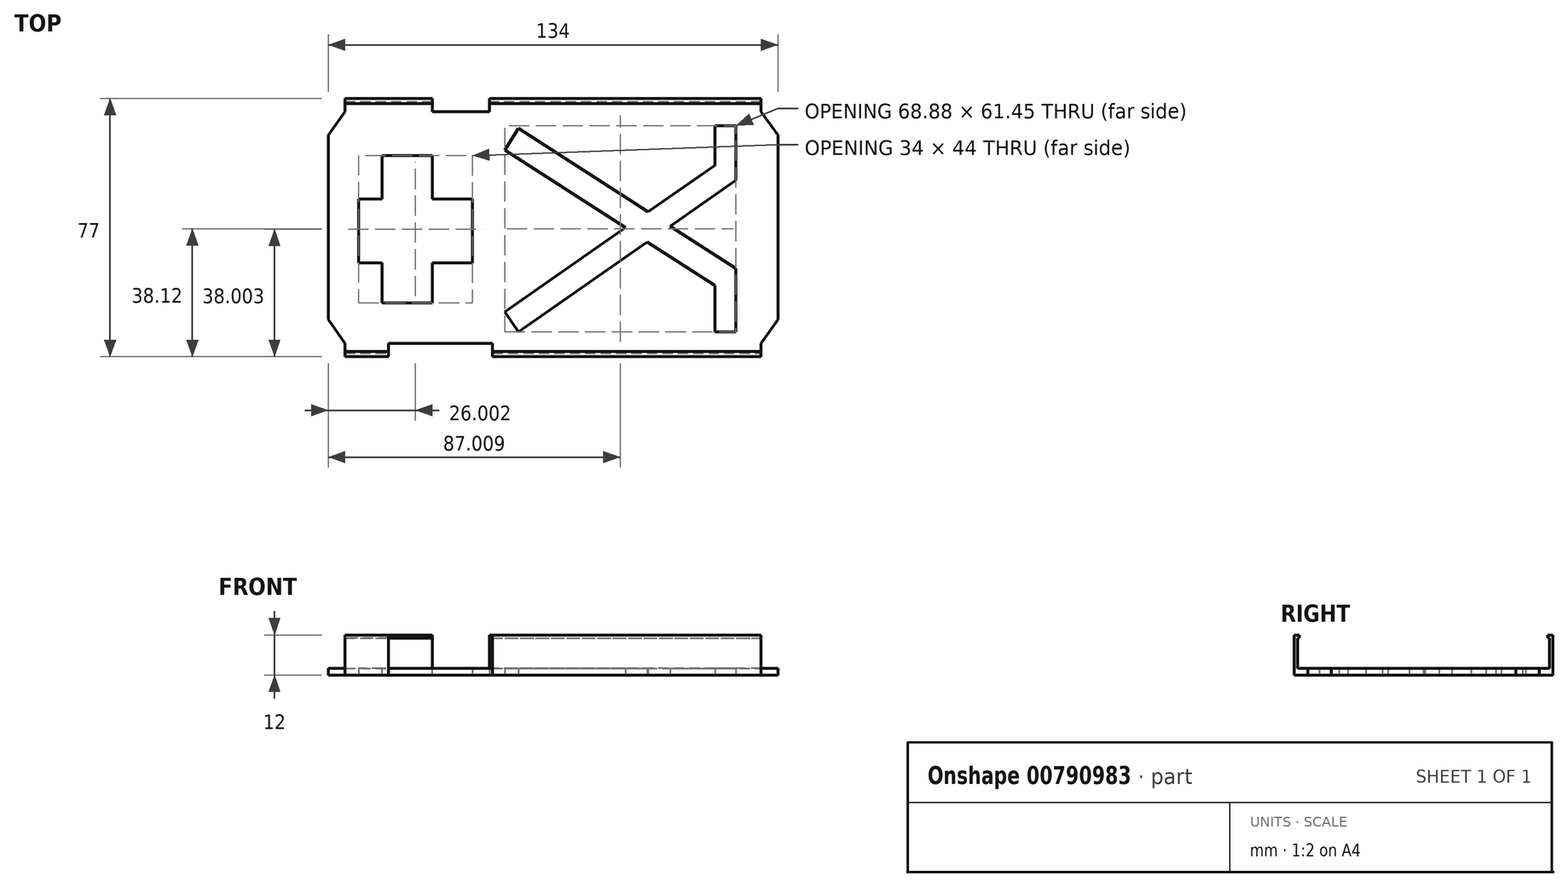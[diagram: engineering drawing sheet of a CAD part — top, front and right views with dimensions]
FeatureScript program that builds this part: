
annotation { "Feature Type Name" : "Feature", "Feature Type Description" : "" }
export const myFeature = defineFeature(function(context is Context, id is Id, definition is map)
    precondition{}
    {
        {
            var Q0;
            Q0=qCreatedBy(makeId("Top.planeOp"),FACE);
            var sketch = newSketch(context, id + "F0", { "sketchPlane" : qUnion([Q0])});
            skLineSegment(sketch, "E0.bottom", {"start": v(-71.89, 59.7) * mm, "end": v(62.11, 59.7) * mm});
            skLineSegment(sketch, "E0.top", {"start": v(-71.89, -9.3) * mm, "end": v(62.11, -9.3) * mm});
            skLineSegment(sketch, "E0.left", {"start": v(-71.89, 59.7) * mm, "end": v(-71.89, -9.3) * mm});
            skLineSegment(sketch, "E0.right", {"start": v(62.11, 59.7) * mm, "end": v(62.11, -9.3) * mm});
            skPoint(sketch, "E1", {"position": v(-71.89, 25.2) * mm});
            skSolve(sketch);
        }
        {
            var Q0;
            Q0=makeQuery(id+"F0.imprint","IMPRINT",FACE,{"disambiguationData":[TD([[makeQuery(id+"F0.imprint","IMPRINT",EDGE,{"derivedFrom":sQuery(id+"F0.wireOp",EDGE,"E0.bottom")}),-1.0]])]});
            extrude(context, id + "F1", {"entities" : qUnion([Q0]), "depth" : 2 * mm, "offsetDistance" : 25 * mm});
        }
        {
            var Q0;
            Q0=makeQuery(id+"F1.opExtrude","SWEPT_FACE",FACE,{"disambiguationData":[OSD([sQuery(id+"F0.wireOp",EDGE,"E0.top")])]});
            var sketch = newSketch(context, id + "F2", { "sketchPlane" : qUnion([Q0])});
            skLineSegment(sketch, "E2.bottom", {"start": v(57.11, 2) * mm, "end": v(-23.89, 2) * mm});
            skLineSegment(sketch, "E2.top", {"start": v(57.11, 0) * mm, "end": v(-23.89, 0) * mm});
            skLineSegment(sketch, "E2.left", {"start": v(57.11, 2) * mm, "end": v(57.11, 0) * mm});
            skLineSegment(sketch, "E2.right", {"start": v(-23.89, 2) * mm, "end": v(-23.89, 0) * mm});
            skSolve(sketch);
        }
        {
            var Q0;
            Q0=makeQuery(id+"F2.imprint","IMPRINT",FACE,{"disambiguationData":[TD([[makeQuery(id+"F2.imprint","IMPRINT",EDGE,{"derivedFrom":sQuery(id+"F2.wireOp",EDGE,"E2.bottom")}),-1.0]])]});
            extrude(context, id + "F3", {"entities" : qUnion([Q0]), "operationType" : NewBodyOperationType.ADD, "depth" : 4 * mm, "offsetDistance" : 25 * mm});
        }
        {
            var Q0;
            Q0=makeQuery(id+"F3.boolean.opBoolean","MERGE",FACE,{"derivedFrom":[makeQuery(id+"F1.opExtrude","CAP_FACE",FACE,{"disambiguationData":[OSD([sQuery(id+"F0.wireOp",EDGE,"E0.bottom"),sQuery(id+"F0.wireOp",EDGE,"E0.top"),sQuery(id+"F0.wireOp",EDGE,"E0.left"),sQuery(id+"F0.wireOp",EDGE,"E0.right")])],"isStart":false}),makeQuery(id+"F3.opExtrude","SWEPT_FACE",FACE,{"disambiguationData":[OSD([sQuery(id+"F2.wireOp",EDGE,"E2.bottom")])]})]});
            var sketch = newSketch(context, id + "F4", { "sketchPlane" : qUnion([Q0])});
            skLineSegment(sketch, "E3", {"start": v(-23.89, -9.3) * mm, "end": v(57.11, -9.3) * mm});
            skSolve(sketch);
        }
        {
            var Q0;
            Q0=makeQuery(id+"F4.imprint","IMPRINT",FACE,{"disambiguationData":[TD([[makeQuery(id+"F4.imprint","IMPRINT",EDGE,{"derivedFrom":sQuery(id+"F4.wireOp",EDGE,"E3")}),-1.0]])]});
            extrude(context, id + "F5", {"entities" : qUnion([Q0]), "operationType" : NewBodyOperationType.ADD, "depth" : 3 * mm, "offsetDistance" : 25 * mm});
        }
        {
            var Q0;
            Q0=makeQuery(id+"F5.opExtrude","CAP_FACE",FACE,{"disambiguationData":[OSD([sQuery(id+"F0.wireOp",EDGE,"E0.top"),sQuery(id+"F2.wireOp",EDGE,"E2.bottom"),sQuery(id+"F2.wireOp",EDGE,"E2.left"),sQuery(id+"F2.wireOp",EDGE,"E2.right"),sQuery(id+"F4.wireOp",EDGE,"E3")])],"isStart":false});
            extrude(context, id + "F6", {"entities" : qUnion([Q0]), "operationType" : NewBodyOperationType.ADD, "depth" : 7 * mm, "offsetDistance" : 25 * mm});
        }
        {
            var Q0;
            {var subQ0=sQuery(id+"F4.wireOp",EDGE,"E3");Q0=makeQuery(id+"F6.boolean.opBoolean","MERGE",FACE,{"derivedFrom":[makeQuery(id+"F5.opExtrude","SWEPT_FACE",FACE,{"disambiguationData":[OSD([subQ0])]}),makeQuery(id+"F6.opExtrude","SWEPT_FACE",FACE,{"disambiguationData":[OSD([subQ0])]})]});}
            extrude(context, id + "F7", {"entities" : qUnion([Q0]), "operationType" : NewBodyOperationType.REMOVE, "oppositeDirection" : true, "depth" : 3 * mm, "offsetDistance" : 25 * mm});
        }
        {
            var Q0;
            Q0=makeQuery(id+"F7.boolean.opBoolean","COPY",FACE,{"derivedFrom":makeQuery(id+"F7.opExtrude","CAP_FACE",FACE,{"disambiguationData":[OSD([sQuery(id+"F4.wireOp",EDGE,"E3")])],"isStart":false})});
            var sketch = newSketch(context, id + "F8", { "sketchPlane" : qUnion([Q0])});
            skLineSegment(sketch, "E4", {"start": v(-57.11, 12) * mm, "end": v(23.89, 12) * mm});
            skLineSegment(sketch, "E5", {"start": v(23.89, 12) * mm, "end": v(23.89, 11) * mm});
            skLineSegment(sketch, "E6", {"start": v(23.89, 11) * mm, "end": v(-57.11, 11) * mm});
            skLineSegment(sketch, "E7", {"start": v(-57.11, 11) * mm, "end": v(-57.11, 12) * mm});
            skSolve(sketch);
        }
        {
            var Q0;
            Q0=makeQuery(id+"F8.imprint","IMPRINT",FACE,{"disambiguationData":[TD([[makeQuery(id+"F8.imprint","IMPRINT",EDGE,{"derivedFrom":sQuery(id+"F8.wireOp",EDGE,"E4")}),1.0]])]});
            extrude(context, id + "F9", {"entities" : qUnion([Q0]), "operationType" : NewBodyOperationType.ADD, "depth" : 0.5 * mm, "offsetDistance" : 25 * mm});
        }
        {
            var Q0;
            {var subQ0=sQuery(id+"F2.wireOp",EDGE,"E2.right");var subQ1=sQuery(id+"F2.wireOp",EDGE,"E2.bottom");var subQ2=sQuery(id+"F0.wireOp",EDGE,"E0.top");Q0=makeQuery(id+"F9.boolean.opBoolean","MERGE",FACE,{"derivedFrom":[makeQuery(id+"F6.boolean.opBoolean","MERGE",FACE,{"derivedFrom":[makeQuery(id+"F5.boolean.opBoolean","MERGE",FACE,{"derivedFrom":[makeQuery(id+"F3.opExtrude","SWEPT_FACE",FACE,{"disambiguationData":[OSD([subQ0])]}),makeQuery(id+"F5.opExtrude","SWEPT_FACE",FACE,{"disambiguationData":[OSD([subQ2,subQ1,subQ0])]})]}),makeQuery(id+"F6.opExtrude","SWEPT_FACE",FACE,{"disambiguationData":[OSD([subQ2,subQ1,subQ0])]})]}),makeQuery(id+"F9.opExtrude","SWEPT_FACE",FACE,{"disambiguationData":[OSD([sQuery(id+"F8.wireOp",EDGE,"zQEFb7VZ-tBJw-V2n3-Wt8e-xeAuR17gCr9D.right")])]})]});}
            extrude(context, id + "F10", {"entities" : qUnion([Q0]), "operationType" : NewBodyOperationType.REMOVE, "oppositeDirection" : true, "depth" : 1 * mm, "offsetDistance" : 25 * mm});
        }
        {
            var Q0;
            {var subQ0=sQuery(id+"F2.wireOp",EDGE,"E2.right");var subQ2=sQuery(id+"F0.wireOp",EDGE,"E0.left");var subQ3=sQuery(id+"F0.wireOp",EDGE,"E0.top");Q0=makeQuery(id+"F10.boolean.opBoolean","MERGE",FACE,{"derivedFrom":[makeQuery(id+"F3.boolean.opBoolean","SPLIT",FACE,{"disambiguationData":[TD([makeQuery(id+"F1.opExtrude","SWEPT_FACE",FACE,{"disambiguationData":[OSD([subQ2])]})])],"derivedFrom":makeQuery(id+"F1.opExtrude","SWEPT_FACE",FACE,{"disambiguationData":[OSD([subQ3])]})}),makeQuery(id+"F10.opExtrude","SWEPT_FACE",FACE,{"disambiguationData":[OSD([subQ0])]})]});}
            var sketch = newSketch(context, id + "F11", { "sketchPlane" : qUnion([Q0])});
            skLineSegment(sketch, "E8.bottom", {"start": v(-66.89, 2) * mm, "end": v(-53.89, 2) * mm});
            skLineSegment(sketch, "E8.top", {"start": v(-66.89, 0) * mm, "end": v(-53.89, 0) * mm});
            skLineSegment(sketch, "E8.left", {"start": v(-66.89, 2) * mm, "end": v(-66.89, 0) * mm});
            skLineSegment(sketch, "E8.right", {"start": v(-53.89, 2) * mm, "end": v(-53.89, 0) * mm});
            skSolve(sketch);
        }
        {
            var Q0;
            Q0=makeQuery(id+"F11.imprint","IMPRINT",FACE,{"disambiguationData":[TD([[makeQuery(id+"F11.imprint","IMPRINT",EDGE,{"derivedFrom":sQuery(id+"F11.wireOp",EDGE,"E8.bottom")}),-1.0]])]});
            extrude(context, id + "F12", {"entities" : qUnion([Q0]), "operationType" : NewBodyOperationType.ADD, "depth" : 4 * mm, "offsetDistance" : 25 * mm});
        }
        {
            var Q0;
            {var subQ0=sQuery(id+"F4.wireOp",EDGE,"E3");Q0=makeQuery(id+"F12.boolean.opBoolean","MERGE",FACE,{"derivedFrom":[makeQuery(id+"F7.boolean.opBoolean","MERGE",FACE,{"derivedFrom":[makeQuery(id+"F3.boolean.opBoolean","MERGE",FACE,{"derivedFrom":[makeQuery(id+"F1.opExtrude","CAP_FACE",FACE,{"disambiguationData":[OSD([sQuery(id+"F0.wireOp",EDGE,"E0.bottom"),sQuery(id+"F0.wireOp",EDGE,"E0.top"),sQuery(id+"F0.wireOp",EDGE,"E0.left"),sQuery(id+"F0.wireOp",EDGE,"E0.right")])],"isStart":false}),makeQuery(id+"F3.opExtrude","SWEPT_FACE",FACE,{"disambiguationData":[OSD([sQuery(id+"F2.wireOp",EDGE,"E2.bottom")])]})]}),makeQuery(id+"F7.opExtrude","SWEPT_FACE",FACE,{"disambiguationData":[OSD([subQ0]),TDD([makeQuery(id+"F5.opExtrude","CAP_EDGE",EDGE,{"disambiguationData":[OSD([subQ0])],"isStart":true})])]})]}),makeQuery(id+"F12.opExtrude","SWEPT_FACE",FACE,{"disambiguationData":[OSD([sQuery(id+"F11.wireOp",EDGE,"E8.bottom")])]})]});}
            var sketch = newSketch(context, id + "F13", { "sketchPlane" : qUnion([Q0])});
            skLineSegment(sketch, "E9", {"start": v(-66.89, -9.3) * mm, "end": v(-53.89, -9.3) * mm});
            skSolve(sketch);
        }
        {
            var Q0;
            Q0=makeQuery(id+"F13.imprint","IMPRINT",FACE,{"disambiguationData":[TD([[makeQuery(id+"F13.imprint","IMPRINT",EDGE,{"derivedFrom":sQuery(id+"F13.wireOp",EDGE,"E9")}),-1.0]])]});
            extrude(context, id + "F14", {"entities" : qUnion([Q0]), "operationType" : NewBodyOperationType.ADD, "depth" : 10 * mm, "offsetDistance" : 25 * mm});
        }
        {
            var Q0;
            Q0=makeQuery(id+"F14.opExtrude","SWEPT_FACE",FACE,{"disambiguationData":[OSD([sQuery(id+"F13.wireOp",EDGE,"E9")])]});
            extrude(context, id + "F15", {"entities" : qUnion([Q0]), "operationType" : NewBodyOperationType.REMOVE, "oppositeDirection" : true, "depth" : 3 * mm, "offsetDistance" : 25 * mm});
        }
        {
            var Q0;
            Q0=makeQuery(id+"F15.boolean.opBoolean","COPY",FACE,{"derivedFrom":makeQuery(id+"F15.opExtrude","CAP_FACE",FACE,{"disambiguationData":[OSD([sQuery(id+"F13.wireOp",EDGE,"E9")])],"isStart":false})});
            var sketch = newSketch(context, id + "F16", { "sketchPlane" : qUnion([Q0])});
            skLineSegment(sketch, "E10.bottom", {"start": v(53.89, 12) * mm, "end": v(66.89, 12) * mm});
            skLineSegment(sketch, "E10.top", {"start": v(53.89, 11) * mm, "end": v(66.89, 11) * mm});
            skLineSegment(sketch, "E10.left", {"start": v(53.89, 12) * mm, "end": v(53.89, 11) * mm});
            skLineSegment(sketch, "E10.right", {"start": v(66.89, 12) * mm, "end": v(66.89, 11) * mm});
            skSolve(sketch);
        }
        {
            var Q0;
            Q0=makeQuery(id+"F16.imprint","IMPRINT",FACE,{"disambiguationData":[TD([[makeQuery(id+"F16.imprint","IMPRINT",EDGE,{"derivedFrom":sQuery(id+"F16.wireOp",EDGE,"E10.bottom")}),1.0]])]});
            extrude(context, id + "F17", {"entities" : qUnion([Q0]), "operationType" : NewBodyOperationType.ADD, "depth" : 0.5 * mm, "offsetDistance" : 25 * mm});
        }
        {
            var Q0;
            Q0=makeQuery(id+"F1.opExtrude","SWEPT_FACE",FACE,{"disambiguationData":[OSD([sQuery(id+"F0.wireOp",EDGE,"E0.bottom")])]});
            var sketch = newSketch(context, id + "F18", { "sketchPlane" : qUnion([Q0])});
            skLineSegment(sketch, "E11.bottom", {"start": v(-57.11, 2) * mm, "end": v(23.89, 2) * mm});
            skLineSegment(sketch, "E11.top", {"start": v(-57.11, 0) * mm, "end": v(23.89, 0) * mm});
            skLineSegment(sketch, "E11.left", {"start": v(-57.11, 2) * mm, "end": v(-57.11, 0) * mm});
            skLineSegment(sketch, "E11.right", {"start": v(23.89, 2) * mm, "end": v(23.89, 0) * mm});
            skSolve(sketch);
        }
        {
            var Q0;
            Q0=makeQuery(id+"F18.imprint","IMPRINT",FACE,{"disambiguationData":[TD([[makeQuery(id+"F18.imprint","IMPRINT",EDGE,{"derivedFrom":sQuery(id+"F18.wireOp",EDGE,"E11.bottom")}),1.0]])]});
            extrude(context, id + "F19", {"entities" : qUnion([Q0]), "operationType" : NewBodyOperationType.ADD, "depth" : 4 * mm, "offsetDistance" : 25 * mm});
        }
        {
            var Q0;
            {var subQ0=sQuery(id+"F13.wireOp",EDGE,"E9");var subQ1=sQuery(id+"F4.wireOp",EDGE,"E3");Q0=makeQuery(id+"F19.boolean.opBoolean","MERGE",FACE,{"derivedFrom":[makeQuery(id+"F15.boolean.opBoolean","MERGE",FACE,{"derivedFrom":[makeQuery(id+"F12.boolean.opBoolean","MERGE",FACE,{"derivedFrom":[makeQuery(id+"F7.boolean.opBoolean","MERGE",FACE,{"derivedFrom":[makeQuery(id+"F3.boolean.opBoolean","MERGE",FACE,{"derivedFrom":[makeQuery(id+"F1.opExtrude","CAP_FACE",FACE,{"disambiguationData":[OSD([sQuery(id+"F0.wireOp",EDGE,"E0.bottom"),sQuery(id+"F0.wireOp",EDGE,"E0.top"),sQuery(id+"F0.wireOp",EDGE,"E0.left"),sQuery(id+"F0.wireOp",EDGE,"E0.right")])],"isStart":false}),makeQuery(id+"F3.opExtrude","SWEPT_FACE",FACE,{"disambiguationData":[OSD([sQuery(id+"F2.wireOp",EDGE,"E2.bottom")])]})]}),makeQuery(id+"F7.opExtrude","SWEPT_FACE",FACE,{"disambiguationData":[OSD([subQ1]),TDD([makeQuery(id+"F5.opExtrude","CAP_EDGE",EDGE,{"disambiguationData":[OSD([subQ1])],"isStart":true})])]})]}),makeQuery(id+"F12.opExtrude","SWEPT_FACE",FACE,{"disambiguationData":[OSD([sQuery(id+"F11.wireOp",EDGE,"E8.bottom")])]})]}),makeQuery(id+"F15.opExtrude","SWEPT_FACE",FACE,{"disambiguationData":[OSD([subQ0]),TDD([makeQuery(id+"F14.opExtrude","CAP_EDGE",EDGE,{"disambiguationData":[OSD([subQ0])],"isStart":true})])]})]}),makeQuery(id+"F19.opExtrude","SWEPT_FACE",FACE,{"disambiguationData":[OSD([sQuery(id+"F18.wireOp",EDGE,"E11.bottom")])]})]});}
            var sketch = newSketch(context, id + "F20", { "sketchPlane" : qUnion([Q0])});
            skLineSegment(sketch, "E12", {"start": v(57.11, 59.7) * mm, "end": v(-23.89, 59.7) * mm});
            skSolve(sketch);
        }
        {
            var Q0;
            Q0=makeQuery(id+"F20.imprint","IMPRINT",FACE,{"disambiguationData":[TD([[makeQuery(id+"F20.imprint","IMPRINT",EDGE,{"derivedFrom":sQuery(id+"F20.wireOp",EDGE,"E12")}),-1.0]])]});
            extrude(context, id + "F21", {"entities" : qUnion([Q0]), "operationType" : NewBodyOperationType.ADD, "depth" : 10 * mm, "offsetDistance" : 25 * mm});
        }
        {
            var Q0;
            Q0=makeQuery(id+"F21.opExtrude","SWEPT_FACE",FACE,{"disambiguationData":[OSD([sQuery(id+"F20.wireOp",EDGE,"E12")])]});
            extrude(context, id + "F22", {"entities" : qUnion([Q0]), "operationType" : NewBodyOperationType.REMOVE, "oppositeDirection" : true, "depth" : 3 * mm, "offsetDistance" : 25 * mm});
        }
        {
            var Q0;
            Q0=makeQuery(id+"F22.boolean.opBoolean","COPY",FACE,{"derivedFrom":makeQuery(id+"F22.opExtrude","CAP_FACE",FACE,{"disambiguationData":[OSD([sQuery(id+"F20.wireOp",EDGE,"E12")])],"isStart":false})});
            var sketch = newSketch(context, id + "F23", { "sketchPlane" : qUnion([Q0])});
            skLineSegment(sketch, "E13.bottom", {"start": v(-23.89, 12) * mm, "end": v(57.11, 12) * mm});
            skLineSegment(sketch, "E13.top", {"start": v(-23.89, 11) * mm, "end": v(57.11, 11) * mm});
            skLineSegment(sketch, "E13.left", {"start": v(-23.89, 12) * mm, "end": v(-23.89, 11) * mm});
            skLineSegment(sketch, "E13.right", {"start": v(57.11, 12) * mm, "end": v(57.11, 11) * mm});
            skSolve(sketch);
        }
        {
            var Q0;
            Q0=makeQuery(id+"F23.imprint","IMPRINT",FACE,{"disambiguationData":[TD([[makeQuery(id+"F23.imprint","IMPRINT",EDGE,{"derivedFrom":sQuery(id+"F23.wireOp",EDGE,"E13.bottom")}),1.0]])]});
            extrude(context, id + "F24", {"entities" : qUnion([Q0]), "operationType" : NewBodyOperationType.ADD, "depth" : 0.5 * mm, "offsetDistance" : 25 * mm});
        }
        {
            var Q0;
            {var subQ3=sQuery(id+"F0.wireOp",EDGE,"E0.left");var subQ5=sQuery(id+"F0.wireOp",EDGE,"E0.bottom");Q0=makeQuery(id+"F19.boolean.opBoolean","SPLIT",FACE,{"disambiguationData":[TD([makeQuery(id+"F1.opExtrude","SWEPT_FACE",FACE,{"disambiguationData":[OSD([subQ3])]})])],"derivedFrom":makeQuery(id+"F1.opExtrude","SWEPT_FACE",FACE,{"disambiguationData":[OSD([subQ5])]})});}
            var sketch = newSketch(context, id + "F25", { "sketchPlane" : qUnion([Q0])});
            skLineSegment(sketch, "E14.bottom", {"start": v(66.89, 2) * mm, "end": v(40.89, 2) * mm});
            skLineSegment(sketch, "E14.top", {"start": v(66.89, 0) * mm, "end": v(40.89, 0) * mm});
            skLineSegment(sketch, "E14.left", {"start": v(66.89, 2) * mm, "end": v(66.89, 0) * mm});
            skLineSegment(sketch, "E14.right", {"start": v(40.89, 2) * mm, "end": v(40.89, 0) * mm});
            skSolve(sketch);
        }
        {
            var Q0;
            Q0=makeQuery(id+"F25.imprint","IMPRINT",FACE,{"disambiguationData":[TD([[makeQuery(id+"F25.imprint","IMPRINT",EDGE,{"derivedFrom":sQuery(id+"F25.wireOp",EDGE,"E14.bottom")}),1.0]])]});
            extrude(context, id + "F26", {"entities" : qUnion([Q0]), "operationType" : NewBodyOperationType.ADD, "depth" : 4 * mm, "offsetDistance" : 25 * mm});
        }
        {
            var Q0;
            {var subQ0=sQuery(id+"F20.wireOp",EDGE,"E12");var subQ1=sQuery(id+"F13.wireOp",EDGE,"E9");var subQ2=sQuery(id+"F4.wireOp",EDGE,"E3");Q0=makeQuery(id+"F26.boolean.opBoolean","MERGE",FACE,{"derivedFrom":[makeQuery(id+"F22.boolean.opBoolean","MERGE",FACE,{"derivedFrom":[makeQuery(id+"F19.boolean.opBoolean","MERGE",FACE,{"derivedFrom":[makeQuery(id+"F15.boolean.opBoolean","MERGE",FACE,{"derivedFrom":[makeQuery(id+"F12.boolean.opBoolean","MERGE",FACE,{"derivedFrom":[makeQuery(id+"F7.boolean.opBoolean","MERGE",FACE,{"derivedFrom":[makeQuery(id+"F3.boolean.opBoolean","MERGE",FACE,{"derivedFrom":[makeQuery(id+"F1.opExtrude","CAP_FACE",FACE,{"disambiguationData":[OSD([sQuery(id+"F0.wireOp",EDGE,"E0.bottom"),sQuery(id+"F0.wireOp",EDGE,"E0.top"),sQuery(id+"F0.wireOp",EDGE,"E0.left"),sQuery(id+"F0.wireOp",EDGE,"E0.right")])],"isStart":false}),makeQuery(id+"F3.opExtrude","SWEPT_FACE",FACE,{"disambiguationData":[OSD([sQuery(id+"F2.wireOp",EDGE,"E2.bottom")])]})]}),makeQuery(id+"F7.opExtrude","SWEPT_FACE",FACE,{"disambiguationData":[OSD([subQ2]),TDD([makeQuery(id+"F5.opExtrude","CAP_EDGE",EDGE,{"disambiguationData":[OSD([subQ2])],"isStart":true})])]})]}),makeQuery(id+"F12.opExtrude","SWEPT_FACE",FACE,{"disambiguationData":[OSD([sQuery(id+"F11.wireOp",EDGE,"E8.bottom")])]})]}),makeQuery(id+"F15.opExtrude","SWEPT_FACE",FACE,{"disambiguationData":[OSD([subQ1]),TDD([makeQuery(id+"F14.opExtrude","CAP_EDGE",EDGE,{"disambiguationData":[OSD([subQ1])],"isStart":true})])]})]}),makeQuery(id+"F19.opExtrude","SWEPT_FACE",FACE,{"disambiguationData":[OSD([sQuery(id+"F18.wireOp",EDGE,"E11.bottom")])]})]}),makeQuery(id+"F22.opExtrude","SWEPT_FACE",FACE,{"disambiguationData":[OSD([subQ0]),TDD([makeQuery(id+"F21.opExtrude","CAP_EDGE",EDGE,{"disambiguationData":[OSD([subQ0])],"isStart":true})])]})]}),makeQuery(id+"F26.opExtrude","SWEPT_FACE",FACE,{"disambiguationData":[OSD([sQuery(id+"F25.wireOp",EDGE,"E14.bottom")])]})]});}
            var sketch = newSketch(context, id + "F27", { "sketchPlane" : qUnion([Q0])});
            skLineSegment(sketch, "E15", {"start": v(-40.89, 59.7) * mm, "end": v(-66.89, 59.7) * mm});
            skSolve(sketch);
        }
        {
            var Q0;
            Q0=makeQuery(id+"F27.imprint","IMPRINT",FACE,{"disambiguationData":[TD([[makeQuery(id+"F27.imprint","IMPRINT",EDGE,{"derivedFrom":sQuery(id+"F27.wireOp",EDGE,"E15")}),-1.0]])]});
            extrude(context, id + "F28", {"entities" : qUnion([Q0]), "operationType" : NewBodyOperationType.ADD, "depth" : 10 * mm, "offsetDistance" : 25 * mm});
        }
        {
            var Q0;
            Q0=makeQuery(id+"F28.opExtrude","SWEPT_FACE",FACE,{"disambiguationData":[OSD([sQuery(id+"F27.wireOp",EDGE,"E15")])]});
            extrude(context, id + "F29", {"entities" : qUnion([Q0]), "operationType" : NewBodyOperationType.REMOVE, "oppositeDirection" : true, "depth" : 3 * mm, "offsetDistance" : 25 * mm});
        }
        {
            var Q0;
            Q0=makeQuery(id+"F29.boolean.opBoolean","COPY",FACE,{"derivedFrom":makeQuery(id+"F29.opExtrude","CAP_FACE",FACE,{"disambiguationData":[OSD([sQuery(id+"F27.wireOp",EDGE,"E15")])],"isStart":false})});
            var sketch = newSketch(context, id + "F30", { "sketchPlane" : qUnion([Q0])});
            skLineSegment(sketch, "E16.bottom", {"start": v(-66.89, 12) * mm, "end": v(-40.89, 12) * mm});
            skLineSegment(sketch, "E16.top", {"start": v(-66.89, 11) * mm, "end": v(-40.89, 11) * mm});
            skLineSegment(sketch, "E16.left", {"start": v(-66.89, 12) * mm, "end": v(-66.89, 11) * mm});
            skLineSegment(sketch, "E16.right", {"start": v(-40.89, 12) * mm, "end": v(-40.89, 11) * mm});
            skSolve(sketch);
        }
        {
            var Q0;
            Q0=makeQuery(id+"F30.imprint","IMPRINT",FACE,{"disambiguationData":[TD([[makeQuery(id+"F30.imprint","IMPRINT",EDGE,{"derivedFrom":sQuery(id+"F30.wireOp",EDGE,"E16.bottom")}),1.0]])]});
            extrude(context, id + "F31", {"entities" : qUnion([Q0]), "operationType" : NewBodyOperationType.ADD, "depth" : 0.5 * mm, "offsetDistance" : 25 * mm});
        }
        {
            var Q0;
            {var subQ0=sQuery(id+"F27.wireOp",EDGE,"E15");var subQ1=sQuery(id+"F20.wireOp",EDGE,"E12");var subQ2=sQuery(id+"F13.wireOp",EDGE,"E9");var subQ3=sQuery(id+"F4.wireOp",EDGE,"E3");Q0=makeQuery(id+"F29.boolean.opBoolean","MERGE",FACE,{"derivedFrom":[makeQuery(id+"F26.boolean.opBoolean","MERGE",FACE,{"derivedFrom":[makeQuery(id+"F22.boolean.opBoolean","MERGE",FACE,{"derivedFrom":[makeQuery(id+"F19.boolean.opBoolean","MERGE",FACE,{"derivedFrom":[makeQuery(id+"F15.boolean.opBoolean","MERGE",FACE,{"derivedFrom":[makeQuery(id+"F12.boolean.opBoolean","MERGE",FACE,{"derivedFrom":[makeQuery(id+"F7.boolean.opBoolean","MERGE",FACE,{"derivedFrom":[makeQuery(id+"F3.boolean.opBoolean","MERGE",FACE,{"derivedFrom":[makeQuery(id+"F1.opExtrude","CAP_FACE",FACE,{"disambiguationData":[OSD([sQuery(id+"F0.wireOp",EDGE,"E0.bottom"),sQuery(id+"F0.wireOp",EDGE,"E0.top"),sQuery(id+"F0.wireOp",EDGE,"E0.left"),sQuery(id+"F0.wireOp",EDGE,"E0.right")])],"isStart":false}),makeQuery(id+"F3.opExtrude","SWEPT_FACE",FACE,{"disambiguationData":[OSD([sQuery(id+"F2.wireOp",EDGE,"E2.bottom")])]})]}),makeQuery(id+"F7.opExtrude","SWEPT_FACE",FACE,{"disambiguationData":[OSD([subQ3]),TDD([makeQuery(id+"F5.opExtrude","CAP_EDGE",EDGE,{"disambiguationData":[OSD([subQ3])],"isStart":true})])]})]}),makeQuery(id+"F12.opExtrude","SWEPT_FACE",FACE,{"disambiguationData":[OSD([sQuery(id+"F11.wireOp",EDGE,"E8.bottom")])]})]}),makeQuery(id+"F15.opExtrude","SWEPT_FACE",FACE,{"disambiguationData":[OSD([subQ2]),TDD([makeQuery(id+"F14.opExtrude","CAP_EDGE",EDGE,{"disambiguationData":[OSD([subQ2])],"isStart":true})])]})]}),makeQuery(id+"F19.opExtrude","SWEPT_FACE",FACE,{"disambiguationData":[OSD([sQuery(id+"F18.wireOp",EDGE,"E11.bottom")])]})]}),makeQuery(id+"F22.opExtrude","SWEPT_FACE",FACE,{"disambiguationData":[OSD([subQ1]),TDD([makeQuery(id+"F21.opExtrude","CAP_EDGE",EDGE,{"disambiguationData":[OSD([subQ1])],"isStart":true})])]})]}),makeQuery(id+"F26.opExtrude","SWEPT_FACE",FACE,{"disambiguationData":[OSD([sQuery(id+"F25.wireOp",EDGE,"E14.bottom")])]})]}),makeQuery(id+"F29.opExtrude","SWEPT_FACE",FACE,{"disambiguationData":[OSD([subQ0]),TDD([makeQuery(id+"F28.opExtrude","CAP_EDGE",EDGE,{"disambiguationData":[OSD([subQ0])],"isStart":true})])]})]});}
            var sketch = newSketch(context, id + "F32", { "sketchPlane" : qUnion([Q0])});
            skLineSegment(sketch, "E17", {"start": v(-66.89, 59.7) * mm, "end": v(-71.89, 52.7) * mm});
            skLineSegment(sketch, "E18", {"start": v(-71.89, 52.7) * mm, "end": v(-71.89, 59.7) * mm});
            skLineSegment(sketch, "E19", {"start": v(-71.89, 59.7) * mm, "end": v(-66.89, 59.7) * mm});
            skLineSegment(sketch, "E20", {"start": v(-66.89, -9.3) * mm, "end": v(-71.89, -2.3) * mm});
            skLineSegment(sketch, "E21", {"start": v(-71.89, -2.3) * mm, "end": v(-71.89, -9.3) * mm});
            skLineSegment(sketch, "E22", {"start": v(-71.89, -9.3) * mm, "end": v(-66.89, -9.3) * mm});
            skLineSegment(sketch, "E23", {"start": v(62.11, -9.3) * mm, "end": v(62.11, -2.3) * mm});
            skLineSegment(sketch, "E24", {"start": v(62.11, -2.3) * mm, "end": v(57.11, -9.3) * mm});
            skLineSegment(sketch, "E25", {"start": v(57.11, -9.3) * mm, "end": v(62.11, -9.3) * mm});
            skLineSegment(sketch, "E26", {"start": v(62.11, 59.7) * mm, "end": v(62.11, 52.7) * mm});
            skLineSegment(sketch, "E27", {"start": v(62.11, 52.7) * mm, "end": v(57.11, 59.7) * mm});
            skLineSegment(sketch, "E28", {"start": v(57.11, 59.7) * mm, "end": v(62.11, 59.7) * mm});
            skSolve(sketch);
        }
        {
            var Q0;
            Q0=makeQuery(id+"F32.imprint","IMPRINT",FACE,{"disambiguationData":[TD([[makeQuery(id+"F32.imprint","IMPRINT",EDGE,{"derivedFrom":sQuery(id+"F32.wireOp",EDGE,"E17")}),-1.0]])]});
            var Q1;
            Q1=makeQuery(id+"F32.imprint","IMPRINT",FACE,{"disambiguationData":[TD([[makeQuery(id+"F32.imprint","IMPRINT",EDGE,{"derivedFrom":sQuery(id+"F32.wireOp",EDGE,"E20")}),1.0]])]});
            var Q2;
            Q2=makeQuery(id+"F32.imprint","IMPRINT",FACE,{"disambiguationData":[TD([[makeQuery(id+"F32.imprint","IMPRINT",EDGE,{"derivedFrom":sQuery(id+"F32.wireOp",EDGE,"E23")}),-1.0]])]});
            var Q3;
            Q3=makeQuery(id+"F32.imprint","IMPRINT",FACE,{"disambiguationData":[TD([[makeQuery(id+"F32.imprint","IMPRINT",EDGE,{"derivedFrom":sQuery(id+"F32.wireOp",EDGE,"E26")}),-1.0]])]});
            extrude(context, id + "F33", {"entities" : qUnion([Q0, Q1, Q2, Q3]), "operationType" : NewBodyOperationType.REMOVE, "endBound" : BoundingType.THROUGH_ALL, "oppositeDirection" : true, "depth" : 25 * mm, "offsetDistance" : 25 * mm});
        }
        {
            var Q0;
            Q0=makeQuery(id+"F26.boolean.opBoolean","MERGE",FACE,{"derivedFrom":[makeQuery(id+"F19.boolean.opBoolean","MERGE",FACE,{"derivedFrom":[makeQuery(id+"F12.boolean.opBoolean","MERGE",FACE,{"derivedFrom":[makeQuery(id+"F3.boolean.opBoolean","MERGE",FACE,{"derivedFrom":[makeQuery(id+"F1.opExtrude","CAP_FACE",FACE,{"disambiguationData":[OSD([sQuery(id+"F0.wireOp",EDGE,"E0.bottom"),sQuery(id+"F0.wireOp",EDGE,"E0.top"),sQuery(id+"F0.wireOp",EDGE,"E0.left"),sQuery(id+"F0.wireOp",EDGE,"E0.right")])],"isStart":true}),makeQuery(id+"F3.opExtrude","SWEPT_FACE",FACE,{"disambiguationData":[OSD([sQuery(id+"F2.wireOp",EDGE,"E2.top")])]})]}),makeQuery(id+"F12.opExtrude","SWEPT_FACE",FACE,{"disambiguationData":[OSD([sQuery(id+"F11.wireOp",EDGE,"E8.top")])]})]}),makeQuery(id+"F19.opExtrude","SWEPT_FACE",FACE,{"disambiguationData":[OSD([sQuery(id+"F18.wireOp",EDGE,"E11.top")])]})]}),makeQuery(id+"F26.opExtrude","SWEPT_FACE",FACE,{"disambiguationData":[OSD([sQuery(id+"F25.wireOp",EDGE,"E14.top")])]})]});
            var sketch = newSketch(context, id + "F34", { "sketchPlane" : qUnion([Q0])});
            skLineSegment(sketch, "E29", {"start": v(-66.89, -59.7) * mm, "end": v(-40.89, -59.7) * mm});
            skLineSegment(sketch, "E30", {"start": v(-40.89, -59.7) * mm, "end": v(-23.89, -59.7) * mm});
            skLineSegment(sketch, "E31", {"start": v(-23.89, -59.7) * mm, "end": v(57.11, -59.7) * mm});
            skLineSegment(sketch, "E32", {"start": v(57.11, -59.7) * mm, "end": v(57.11, 9.3) * mm});
            skLineSegment(sketch, "E33", {"start": v(57.11, 9.3) * mm, "end": v(-22.89, 9.3) * mm});
            skLineSegment(sketch, "E34", {"start": v(-22.89, 9.3) * mm, "end": v(-53.89, 9.3) * mm});
            skLineSegment(sketch, "E35", {"start": v(-53.89, 9.3) * mm, "end": v(-66.89, 9.3) * mm});
            skLineSegment(sketch, "E36", {"start": v(-66.89, 9.3) * mm, "end": v(-66.89, -59.7) * mm});
            skLineSegment(sketch, "E37.bottom", {"start": v(-55.89, -46.7) * mm, "end": v(-40.89, -46.7) * mm});
            skLineSegment(sketch, "E37.top", {"start": v(-55.89, -2.7) * mm, "end": v(-40.89, -2.7) * mm});
            skLineSegment(sketch, "E37.left", {"start": v(-55.89, -46.7) * mm, "end": v(-55.89, -2.7) * mm});
            skLineSegment(sketch, "E37.right", {"start": v(-40.89, -46.7) * mm, "end": v(-40.89, -2.7) * mm});
            skPoint(sketch, "E38", {"position": v(-55.89, -33.84) * mm});
            skPoint(sketch, "E39", {"position": v(-62.58, -33.84) * mm});
            skSolve(sketch);
        }
        {
            var Q0;
            Q0=makeQuery(id+"F34.imprint","IMPRINT",FACE,{"disambiguationData":[TD([[makeQuery(id+"F34.imprint","IMPRINT",EDGE,{"derivedFrom":sQuery(id+"F34.wireOp",EDGE,"E37.bottom")}),1.0]])]});
            extrude(context, id + "F35", {"entities" : qUnion([Q0]), "operationType" : NewBodyOperationType.REMOVE, "endBound" : BoundingType.THROUGH_ALL, "oppositeDirection" : true, "depth" : 25 * mm, "offsetDistance" : 25 * mm});
        }
        {
            var Q0;
            Q0=makeQuery(id+"F26.boolean.opBoolean","MERGE",FACE,{"derivedFrom":[makeQuery(id+"F19.boolean.opBoolean","MERGE",FACE,{"derivedFrom":[makeQuery(id+"F12.boolean.opBoolean","MERGE",FACE,{"derivedFrom":[makeQuery(id+"F3.boolean.opBoolean","MERGE",FACE,{"derivedFrom":[makeQuery(id+"F1.opExtrude","CAP_FACE",FACE,{"disambiguationData":[OSD([sQuery(id+"F0.wireOp",EDGE,"E0.bottom"),sQuery(id+"F0.wireOp",EDGE,"E0.top"),sQuery(id+"F0.wireOp",EDGE,"E0.left"),sQuery(id+"F0.wireOp",EDGE,"E0.right")])],"isStart":true}),makeQuery(id+"F3.opExtrude","SWEPT_FACE",FACE,{"disambiguationData":[OSD([sQuery(id+"F2.wireOp",EDGE,"E2.top")])]})]}),makeQuery(id+"F12.opExtrude","SWEPT_FACE",FACE,{"disambiguationData":[OSD([sQuery(id+"F11.wireOp",EDGE,"E8.top")])]})]}),makeQuery(id+"F19.opExtrude","SWEPT_FACE",FACE,{"disambiguationData":[OSD([sQuery(id+"F18.wireOp",EDGE,"E11.top")])]})]}),makeQuery(id+"F26.opExtrude","SWEPT_FACE",FACE,{"disambiguationData":[OSD([sQuery(id+"F25.wireOp",EDGE,"E14.top")])]})]});
            var sketch = newSketch(context, id + "F36", { "sketchPlane" : qUnion([Q0])});
            skLineSegment(sketch, "E40.bottom", {"start": v(-62.89, -33.7) * mm, "end": v(-28.89, -33.7) * mm});
            skLineSegment(sketch, "E40.top", {"start": v(-62.89, -14.7) * mm, "end": v(-28.89, -14.7) * mm});
            skLineSegment(sketch, "E40.left", {"start": v(-62.89, -33.7) * mm, "end": v(-62.89, -14.7) * mm});
            skLineSegment(sketch, "E40.right", {"start": v(-28.89, -33.7) * mm, "end": v(-28.89, -14.7) * mm});
            skPoint(sketch, "E41", {"position": v(-55.89, -33.7) * mm});
            skSolve(sketch);
        }
        {
            var Q0;
            {var subQ0=sQuery(id+"F36.wireOp",EDGE,"E40.left");Q0=makeQuery(id+"F36.imprint","IMPRINT",FACE,{"disambiguationData":[TD([[makeQuery(id+"F36.imprint","IMPRINT",EDGE,{"derivedFrom":subQ0}),-1.0]])]});}
            var Q1;
            {var subQ0=sQuery(id+"F36.wireOp",EDGE,"E40.bottom");var subQ1=makeQuery(id+"F35.boolean.opBoolean","COPY",EDGE,{"derivedFrom":makeQuery(id+"F35.opExtrude","CAP_EDGE",EDGE,{"disambiguationData":[OSD([sQuery(id+"F34.wireOp",EDGE,"E37.left")])],"isStart":true})});var subQ2=makeQuery(id+"F36.imprint","INTERSECT",VERTEX,{"derivedFrom":[subQ1,subQ0]});Q1=makeQuery(id+"F36.imprint","IMPRINT",FACE,{"disambiguationData":[TD([[makeQuery(id+"F36.imprint","IMPRINT",EDGE,{"disambiguationData":[TD([[subQ2,-1.0]])],"derivedFrom":subQ0}),1.0]])]});}
            var Q2;
            {var subQ0=sQuery(id+"F36.wireOp",EDGE,"E40.right");Q2=makeQuery(id+"F36.imprint","IMPRINT",FACE,{"disambiguationData":[TD([[makeQuery(id+"F36.imprint","IMPRINT",EDGE,{"derivedFrom":subQ0}),1.0]])]});}
            extrude(context, id + "F37", {"entities" : qUnion([Q0, Q1, Q2]), "operationType" : NewBodyOperationType.REMOVE, "endBound" : BoundingType.THROUGH_ALL, "oppositeDirection" : true, "depth" : 25 * mm, "offsetDistance" : 25 * mm});
        }
        {
            var Q0;
            Q0=makeQuery(id+"F26.boolean.opBoolean","MERGE",FACE,{"derivedFrom":[makeQuery(id+"F19.boolean.opBoolean","MERGE",FACE,{"derivedFrom":[makeQuery(id+"F12.boolean.opBoolean","MERGE",FACE,{"derivedFrom":[makeQuery(id+"F3.boolean.opBoolean","MERGE",FACE,{"derivedFrom":[makeQuery(id+"F1.opExtrude","CAP_FACE",FACE,{"disambiguationData":[OSD([sQuery(id+"F0.wireOp",EDGE,"E0.bottom"),sQuery(id+"F0.wireOp",EDGE,"E0.top"),sQuery(id+"F0.wireOp",EDGE,"E0.left"),sQuery(id+"F0.wireOp",EDGE,"E0.right")])],"isStart":true}),makeQuery(id+"F3.opExtrude","SWEPT_FACE",FACE,{"disambiguationData":[OSD([sQuery(id+"F2.wireOp",EDGE,"E2.top")])]})]}),makeQuery(id+"F12.opExtrude","SWEPT_FACE",FACE,{"disambiguationData":[OSD([sQuery(id+"F11.wireOp",EDGE,"E8.top")])]})]}),makeQuery(id+"F19.opExtrude","SWEPT_FACE",FACE,{"disambiguationData":[OSD([sQuery(id+"F18.wireOp",EDGE,"E11.top")])]})]}),makeQuery(id+"F26.opExtrude","SWEPT_FACE",FACE,{"disambiguationData":[OSD([sQuery(id+"F25.wireOp",EDGE,"E14.top")])]})]});
            var sketch = newSketch(context, id + "F38", { "sketchPlane" : qUnion([Q0])});
            skSolve(sketch);
        }
        {
            var Q0;
            {var subQ8=sQuery(id+"F2.wireOp",EDGE,"E2.top");Q0=makeQuery(id+"F38.imprint","IMPRINT",FACE,{"disambiguationData":[TD([[makeQuery(id+"F38.imprint","IMPRINT",EDGE,{"derivedFrom":makeQuery(id+"F3.opExtrude","CAP_EDGE",EDGE,{"disambiguationData":[OSD([subQ8])],"isStart":false})}),-1.0]])]});}
            var sketch = newSketch(context, id + "F39", { "sketchPlane" : qUnion([Q0])});
            skLineSegment(sketch, "E42", {"start": v(49.56, -55.54) * mm, "end": v(49.56, -39.28) * mm});
            skLineSegment(sketch, "E43", {"start": v(49.56, -39.28) * mm, "end": v(-15.19, 5.92) * mm});
            skLineSegment(sketch, "E44", {"start": v(-15.19, 5.92) * mm, "end": v(-19.32, 0) * mm});
            skLineSegment(sketch, "E45", {"start": v(-19.32, 0) * mm, "end": v(43.3, -43.72) * mm});
            skLineSegment(sketch, "E46", {"start": v(43.3, -43.72) * mm, "end": v(43.3, -55.54) * mm});
            skLineSegment(sketch, "E47", {"start": v(43.3, -55.54) * mm, "end": v(49.56, -55.54) * mm});
            skLineSegment(sketch, "E48", {"start": v(49.56, -12.94) * mm, "end": v(-15.19, -54.74) * mm});
            skLineSegment(sketch, "E49", {"start": v(-15.19, -54.74) * mm, "end": v(-19.32, -48.34) * mm});
            skLineSegment(sketch, "E50", {"start": v(-19.32, -48.34) * mm, "end": v(43.3, -7.9) * mm});
            skLineSegment(sketch, "E51", {"start": v(43.3, -7.9) * mm, "end": v(43.3, 5.92) * mm});
            skLineSegment(sketch, "E52", {"start": v(43.3, 5.92) * mm, "end": v(49.56, 5.92) * mm});
            skLineSegment(sketch, "E53", {"start": v(49.56, 5.92) * mm, "end": v(49.56, -12.94) * mm});
            skPoint(sketch, "E54", {"position": v(-72, -25.42) * mm});
            skLineSegment(sketch, "E55", {"start": v(-72, -25.42) * mm, "end": v(62.4, -25.42) * mm, "construction": true});
            skSolve(sketch);
        }
        {
            var Q0;
            Q0 = qSketchRegion(id + "F39", true);
            extrude(context, id + "F40", {"entities" : qUnion([Q0]), "operationType" : NewBodyOperationType.REMOVE, "endBound" : BoundingType.THROUGH_ALL, "oppositeDirection" : true, "depth" : 1 * mm, "offsetDistance" : 25 * mm});
        }
    });
